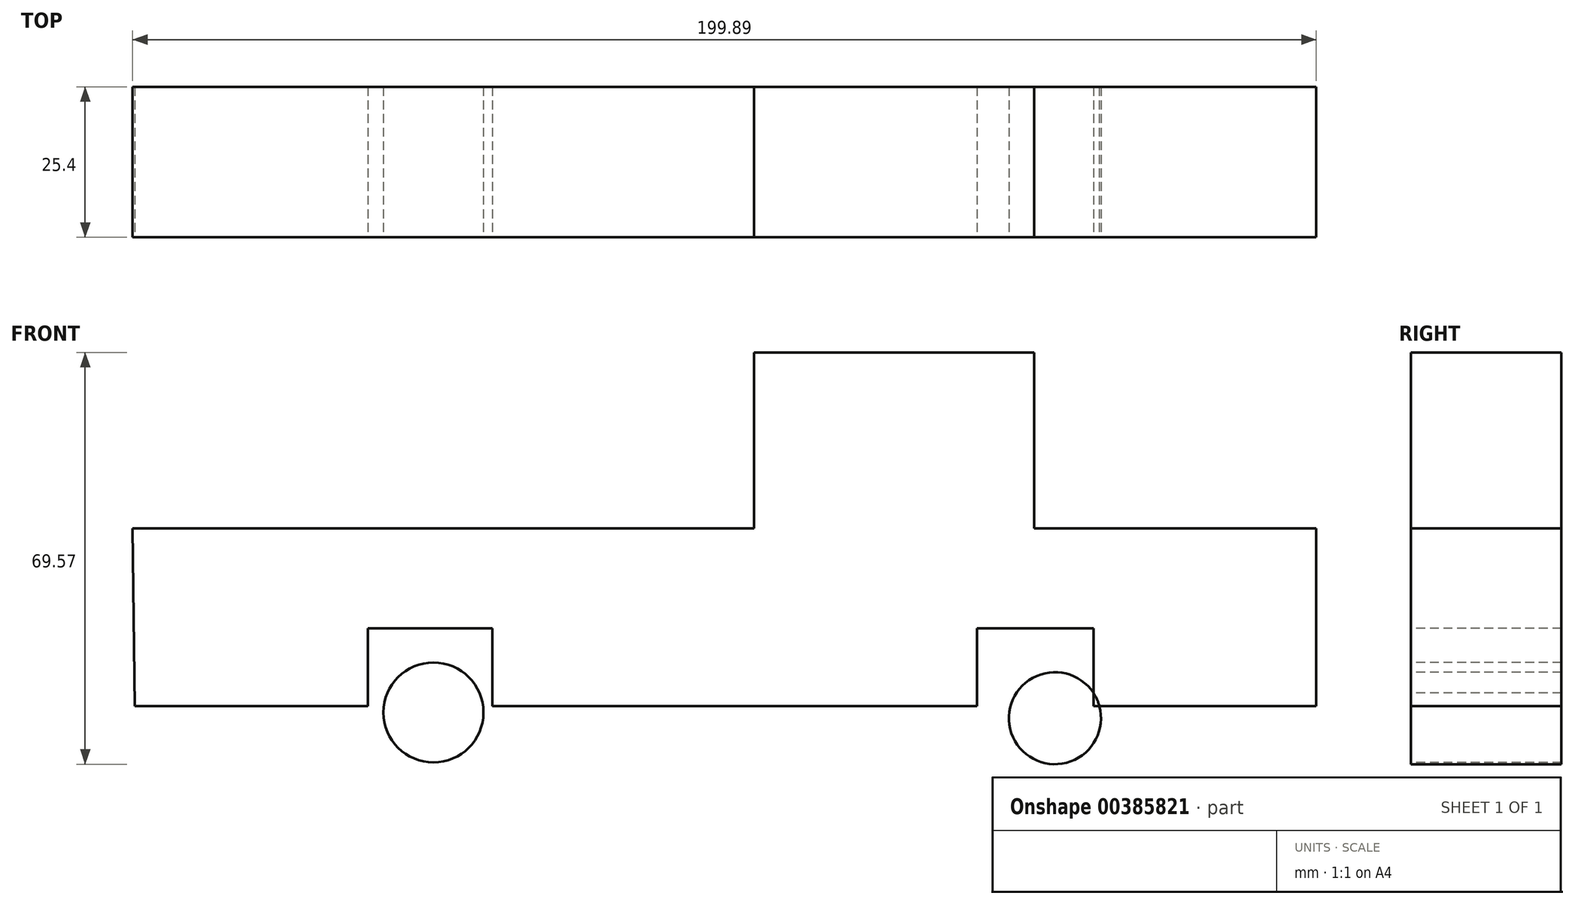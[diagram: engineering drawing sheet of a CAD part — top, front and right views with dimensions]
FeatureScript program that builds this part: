
annotation { "Feature Type Name" : "Feature", "Feature Type Description" : "" }
export const myFeature = defineFeature(function(context is Context, id is Id, definition is map)
    precondition{}
    {
        {
            var Q0;
            Q0=qCreatedBy(makeId("Front.planeOp"),FACE);
            var sketch = newSketch(context, id + "F0", { "sketchPlane" : qUnion([Q0])});
            skLineSegment(sketch, "E0", {"start": v(-116, -59.73) * mm, "end": v(-76.64, -59.73) * mm});
            skLineSegment(sketch, "E1", {"start": v(-76.64, -59.73) * mm, "end": v(-76.64, -46.6) * mm});
            skLineSegment(sketch, "E2", {"start": v(-76.64, -46.6) * mm, "end": v(-55.58, -46.6) * mm});
            skLineSegment(sketch, "E3", {"start": v(-55.58, -46.6) * mm, "end": v(-55.58, -59.73) * mm});
            skLineSegment(sketch, "E4", {"start": v(-55.58, -59.73) * mm, "end": v(26.24, -59.73) * mm});
            skLineSegment(sketch, "E5", {"start": v(26.24, -59.73) * mm, "end": v(26.24, -46.6) * mm});
            skLineSegment(sketch, "E6", {"start": v(26.24, -46.6) * mm, "end": v(45.92, -46.6) * mm});
            skLineSegment(sketch, "E7", {"start": v(45.92, -46.6) * mm, "end": v(45.92, -59.73) * mm});
            skLineSegment(sketch, "E8", {"start": v(45.92, -59.73) * mm, "end": v(83.55, -59.73) * mm});
            skLineSegment(sketch, "E9", {"start": v(83.55, -59.73) * mm, "end": v(83.55, -29.7) * mm});
            skLineSegment(sketch, "E10", {"start": v(83.55, -29.7) * mm, "end": v(35.9, -29.7) * mm});
            skLineSegment(sketch, "E11", {"start": v(35.9, -29.7) * mm, "end": v(35.9, 0) * mm});
            skLineSegment(sketch, "E12", {"start": v(35.9, 0) * mm, "end": v(-11.4, 0) * mm});
            skLineSegment(sketch, "E13", {"start": v(-11.4, 0) * mm, "end": v(-11.4, -29.7) * mm});
            skLineSegment(sketch, "E14", {"start": v(-11.4, -29.7) * mm, "end": v(-116.34, -29.7) * mm});
            skLineSegment(sketch, "E15", {"start": v(-116.34, -29.7) * mm, "end": v(-116, -59.73) * mm});
            skCircle(sketch, "E16", {"center": v(-65.54, -60.83) * mm, "radius": 8.44 * mm});
            skPoint(sketch, "E16.first.point", {"position": v(-69.74, -53.51) * mm});
            skPoint(sketch, "E16.second.point", {"position": v(-62.49, -68.7) * mm});
            skPoint(sketch, "E16.third.point", {"position": v(-58.34, -65.25) * mm});
            skCircle(sketch, "E17", {"center": v(39.42, -61.8) * mm, "radius": 7.78 * mm});
            skPoint(sketch, "E17.first.point", {"position": v(36.6, -54.55) * mm});
            skPoint(sketch, "E17.second.point", {"position": v(32.45, -65.25) * mm});
            skPoint(sketch, "E17.third.point", {"position": v(41.08, -69.4) * mm});
            skSolve(sketch);
        }
        {
            var Q0;
            Q0=makeQuery(id+"F0.imprint","IMPRINT",FACE,{"disambiguationData":[TD([[makeQuery(id+"F0.imprint","IMPRINT",EDGE,{"derivedFrom":sQuery(id+"F0.wireOp",EDGE,"E0")}),1.0]])]});
            var Q1;
            {var subQ0=sQuery(id+"F0.wireOp",EDGE,"E8");var subQ1=sQuery(id+"F0.wireOp",EDGE,"E7");var subQ2=makeQuery(id+"F0.imprint","INTERSECT",VERTEX,{"derivedFrom":[subQ1,subQ0]});Q1=makeQuery(id+"F0.imprint","IMPRINT",FACE,{"disambiguationData":[TD([[makeQuery(id+"F0.imprint","IMPRINT",EDGE,{"disambiguationData":[TD([[subQ2,1.0]])],"derivedFrom":subQ1}),-1.0]])]});}
            var Q2;
            Q2=makeQuery(id+"F0.imprint","IMPRINT",FACE,{"disambiguationData":[TD([[makeQuery(id+"F0.imprint","IMPRINT",EDGE,{"derivedFrom":sQuery(id+"F0.wireOp",EDGE,"E16")}),1.0]])]});
            extrude(context, id + "F1", {"entities" : qUnion([Q0, Q1, Q2]), "oppositeDirection" : true, "depth" : 25.4 * mm});
        }
    });
